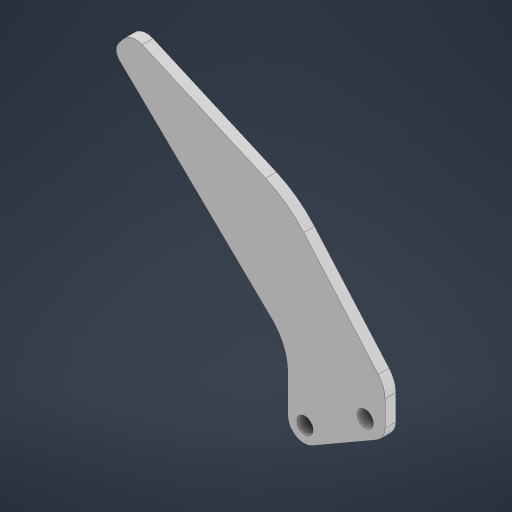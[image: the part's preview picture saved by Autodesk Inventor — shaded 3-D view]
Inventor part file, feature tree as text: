
AUTODESK INVENTOR PART (.ipt)
format: ipt  version: 2023 (Build 270158000, 158)  size: 261,632 bytes
history: native  units: mm
features: extrude x7, fillet x7, sketch x6, chamfer x2
ambient origin geometry x8: Origin, YZ Plane, XZ Plane, XY Plane, X Axis, Y Axis, Z Axis, Center Point
bodies: Solid1 (feature_tree)
feature tree (22):
  extrude  "Extrusion1"  Depth=30.0mm
  fillet  "Fillet1"  [1 undecoded]
  extrude  "Extrusion2"  Depth=3.0mm
  sketch  "Sketch3"  dims[d8=3.0mm d9=21.816616mm]
  extrude  "Extrusion3"  Depth=3.0mm
  extrude  "Extrusion4"  Depth=3.0mm
  fillet  "Fillet2"  Radius=3.0mm
  chamfer  "Chamfer1"  Distance=2.0mm
  fillet  "Fillet3"  Radius=22.68928mm
  extrude  "Extrusion5"  TaperAngle=90.0deg  [1 undecoded]
  fillet  "Fillet4"  Radius=2.0mm
  extrude  "Extrusion6"  Depth=2.0mm TaperAngle=0.0deg
  fillet  "Fillet5"  Radius=10.0mm
  fillet  "Fillet6"  Radius=5.0mm
  chamfer  "Chamfer2"  Distance=20.0mm
  fillet  "Fillet7"  Radius=2.0mm
  extrude  "Extrusion7"  Depth=5.0mm
  sketch  "Sketch1"  dims[d0=18.0mm d1=30.0mm d2=30.0deg]
  sketch  "Sketch2"  dims[d3=2.0mm d4=0.0mm d5=3.0mm]
  sketch  "Sketch4"  dims[d10=6.5mm d11=13.0mm d12=3.0mm]
  sketch  "Sketch5"  dims[d13=3.0mm d14=2.0mm d15=0.0mm d16=22.68928mm]
  sketch  "Sketch6"  dims[d17=50.0mm d18=90.0deg d19=2.0mm d20=0.0mm d21=2.0mm d22=0.0mm d23=10.0mm d24=5.0mm d25=40.0mm d26=45.0deg d27=20.0mm d28=2.0mm d29=0.0mm d30=5.0mm d31=2.0mm d32=0.0mm d33=20.0mm d34=3.0mm d35=20.0mm d36=3.0mm d37=45.0deg d38=2.0mm d39=10.0mm d40=0.0mm]
note: 2 required parameter values undecoded (feature->parameter linkage not recoverable at this tier; creation-order binding heuristic only, values carry confidence <= 0.55)
